# Revit family: MD1-OCRX2X2
name_source: partatom
category: Lighting Fixtures
units: mm (PartAtom-declared; Revit-internal decimal feet)

## family parameters
Always vertical = Yes
Cut with Voids When Loaded = No
Host = Ceiling
Light Source = Yes
OmniClass Number = 23.80.70.11.14.17
OmniClass Title = Direct/Indirect
Part Type = Normal
Room Calculation Point = No
Round Connector Dimension = Use Diameter
Shared = No

## types (5) — shared parameters
Assembly Code = D5020200
Color Filter = 16777215
Description = Patient Room Recessed Ambient Luminaire
Dimming Lamp Color Temperature Shift = <None>
Emit Shape Visible in Rendering = No
Emit from Rectangle Height = 0' - 1 15/32"
Emit from Rectangle Length = 1' - 11 11/16"
Emit from Rectangle Width = 1' - 11 3/4"
Housing Finish = Metal - Viscor - White
Lamp = LED
Length = 1' - 11 11/16"
Lens Depth = 0' - 1 15/32"
Lens Finish = Acrylic - Viscor - Opal White Square
Manufacturer = CERTOLUX by VISCOR
Model = MD1-OCRX
Tilt Angle = 90.00°
URL = https://www.viscor.com
Voltage = 120 V
Width = 1' - 11 3/4"

## per-type parameters (varying)
| type | Apparent Load | Lamp Wattage | Photometric Web File |
| MD1-OCRX 2X2-LED840K030LUNV | 22 VA | 22 VA | MD1-OCRX 2X2-LED840K030LUNV.ies |
| MD1-OCRX 2X2-LED840K040LUNV | 29 VA | 29 VA | MD1-OCRX 2X2-LED840K040LUNV.ies |
| MD1-OCRX 2X2-LED840K050LUNV | 37 VA | 37 VA | MD1-OCRX 2X2-LED840K050LUNV.ies |
| MD1-OCRX 2X2-LED840K060LUNV | 45 VA | 45 VA | MD1-OCRX 2X2-LED840K060LUNV.ies |
| MD1-OCRX 2X2-LED840K075LUNV | 55 VA | 55 VA | MD1-OCRX 2X2-LED840K075LUNV.ies |

## geometry (parser evidence)
native form markers: Sweep x3
no freeform markers — native parametric forms only
